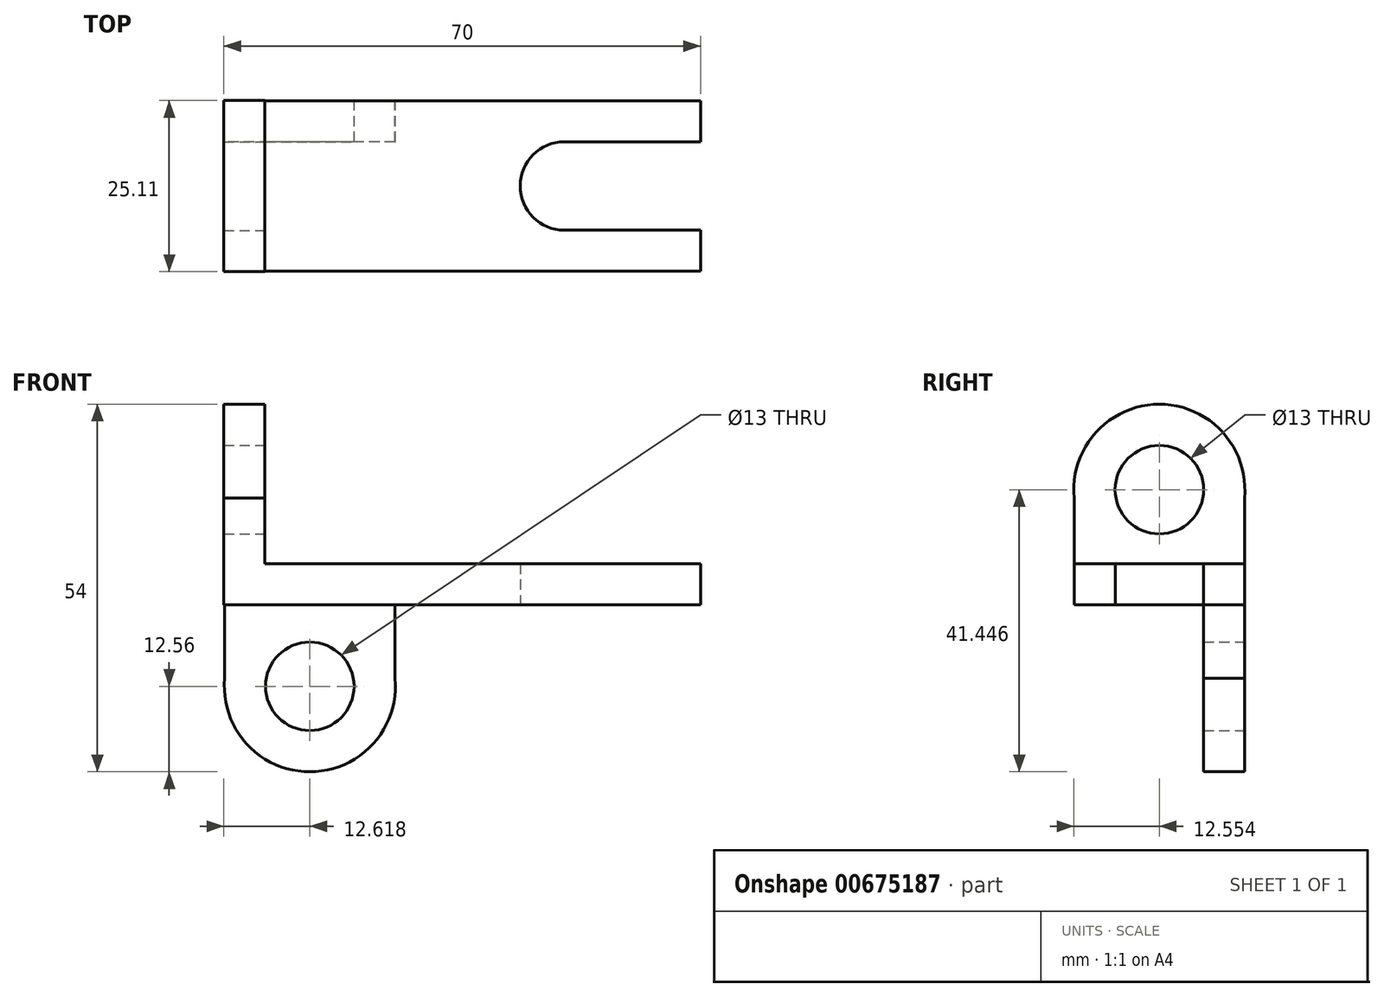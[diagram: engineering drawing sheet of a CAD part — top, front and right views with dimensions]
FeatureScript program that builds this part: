
annotation { "Feature Type Name" : "Feature", "Feature Type Description" : "" }
export const myFeature = defineFeature(function(context is Context, id is Id, definition is map)
    precondition{}
    {
        {
            var Q0;
            Q0=qCreatedBy(makeId("Top.planeOp"),FACE);
            var sketch = newSketch(context, id + "F0", { "sketchPlane" : qUnion([Q0])});
            skLineSegment(sketch, "E0.bottom", {"start": v(-31, 13.84) * mm, "end": v(33, 13.84) * mm});
            skLineSegment(sketch, "E0.top", {"start": v(-31, -11.16) * mm, "end": v(33, -11.16) * mm});
            skLineSegment(sketch, "E0.left", {"start": v(-31, 13.84) * mm, "end": v(-31, -11.16) * mm});
            skLineSegment(sketch, "E0.right", {"start": v(33, 13.84) * mm, "end": v(33, -11.16) * mm});
            skLineSegment(sketch, "E1.bottom", {"start": v(13, 7.86) * mm, "end": v(33, 7.86) * mm});
            skLineSegment(sketch, "E1.top", {"start": v(13, -5.14) * mm, "end": v(33, -5.14) * mm});
            skLineSegment(sketch, "E1.left", {"start": v(13, 7.86) * mm, "end": v(13, -5.14) * mm});
            skLineSegment(sketch, "E1.right", {"start": v(33, 7.86) * mm, "end": v(33, -5.14) * mm});
            skCircle(sketch, "E2", {"center": v(13, 1.36) * mm, "radius": 6.5 * mm});
            skSolve(sketch);
        }
        {
            var Q0;
            Q0=makeQuery(id+"F0.imprint","IMPRINT",FACE,{"disambiguationData":[TD([[makeQuery(id+"F0.imprint","IMPRINT",EDGE,{"derivedFrom":sQuery(id+"F0.wireOp",EDGE,"E0.bottom")}),-1.0]])]});
            var Q1;
            Q1 = qSketchRegion(id + "FkwUM9x7Mz29oJM_1", true);
            extrude(context, id + "F1", {"entities" : qUnion([Q0, Q1]), "depth" : 6 * mm, "offsetDistance" : 25 * mm});
        }
        {
            var Q0;
            Q0=makeQuery(id+"F1.opExtrude","SWEPT_FACE",FACE,{"disambiguationData":[OSD([sQuery(id+"F0.wireOp",EDGE,"E0.left")])]});
            var sketch = newSketch(context, id + "F2", { "sketchPlane" : qUnion([Q0])});
            skLineSegment(sketch, "E3.bottom", {"start": v(11.16, 0) * mm, "end": v(-13.84, 0) * mm});
            skLineSegment(sketch, "E3.top", {"start": v(11.16, 18) * mm, "end": v(-13.84, 18) * mm});
            skLineSegment(sketch, "E3.left", {"start": v(11.16, 0) * mm, "end": v(11.16, 18) * mm});
            skLineSegment(sketch, "E3.right", {"start": v(-13.84, 0) * mm, "end": v(-13.84, 18) * mm});
            skCircle(sketch, "E4", {"center": v(-1.34, 16.89) * mm, "radius": 12.56 * mm});
            skPoint(sketch, "E4.centerSnap0", {"position": v(-1.34, 0) * mm});
            skCircle(sketch, "E5", {"center": v(-1.34, 16.89) * mm, "radius": 6.5 * mm});
            skSolve(sketch);
        }
        {
            var Q0;
            Q0 = qSketchRegion(id + "F2", true);
            extrude(context, id + "F3", {"entities" : qUnion([Q0]), "operationType" : NewBodyOperationType.ADD, "depth" : 6 * mm, "offsetDistance" : 25 * mm});
        }
        {
            var Q0;
            Q0=makeQuery(id+"F1.opExtrude","SWEPT_FACE",FACE,{"disambiguationData":[OSD([sQuery(id+"F0.wireOp",EDGE,"E0.bottom")])]});
            var sketch = newSketch(context, id + "F4", { "sketchPlane" : qUnion([Q0])});
            skLineSegment(sketch, "E6.bottom", {"start": v(11.88, 6) * mm, "end": v(36.88, 6) * mm});
            skLineSegment(sketch, "E6.top", {"start": v(11.88, -12) * mm, "end": v(36.88, -12) * mm});
            skLineSegment(sketch, "E6.left", {"start": v(11.88, 6) * mm, "end": v(11.88, -12) * mm});
            skLineSegment(sketch, "E6.right", {"start": v(36.88, 6) * mm, "end": v(36.88, -12) * mm});
            skCircle(sketch, "E7", {"center": v(24.38, -12) * mm, "radius": 12.56 * mm});
            skCircle(sketch, "E8", {"center": v(24.38, -12) * mm, "radius": 6.5 * mm});
            skSolve(sketch);
        }
        {
            var Q0;
            Q0 = qSketchRegion(id + "F4", true);
            extrude(context, id + "F5", {"entities" : qUnion([Q0]), "operationType" : NewBodyOperationType.ADD, "oppositeDirection" : true, "depth" : 6 * mm, "offsetDistance" : 25 * mm});
        }
    });
